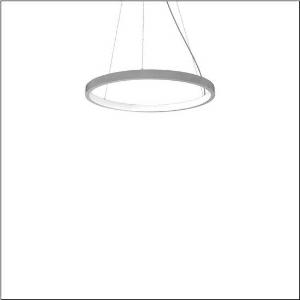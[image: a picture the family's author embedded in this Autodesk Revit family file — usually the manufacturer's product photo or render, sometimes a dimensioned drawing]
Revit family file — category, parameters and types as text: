
# Revit family: silica_21_ring-i_5pjbi2d3204a
name_source: partatom
category: Lighting Fixtures
units: mm (PartAtom-declared; Revit-internal decimal feet)

## family parameters
Cut with Voids When Loaded = No
Host = Face
Light Source = No
Part Type = Normal
Room Calculation Point = No
Round Connector Dimension = Use Diameter
Shared = No

## types (1)
- Silica 21 Ring-I (1 x LED, 5040 lm, 80 W, 4000K)
    Apparent Load = 80 VA
    CIE Flux Codes = 22 48 76 50 101
    Color Rendering = 80
    Color Temperature = 4000K
    Default Elevation = 1800 mm
    Description = Silica 21 Ring-I, suspended luminaire, of PMMA, frosted, light emission: inner ring side luminous distribution, primary light characteristic: symmetric, installation type: suspended mounting, LED, rated luminous flux: 5.040lm, luminous efficacy: 63lm/W, light colour: 840, colour temperature: 4000K, control gear: DALI 2, with terminal, 5-pole, mains connection: 230V, AC/DC, 0/50..60Hz, rated input power: 80W, housing, of extruded aluminium section, metallic grey (RAL 9006), diameter: 805mm, ceiling canopy, metallic grey (RAL 9006), protection rating (lamp compartment): IP40, insulation class (complete): insulation class I (protective earthing), certification: CE, impact resistance: IK02, permissible operating ambient temperature: 0..+35°C, packaging unit: 1 piece
    Height = 48 mm  [stored 0.15748 ft]
    Lamp = 1 x LED
    Lamp Light Flux = 5040 lm
    Lamp Power = 80 W
    Lamp count = 1
    Length = 805 mm
    Luminous efficacy = 63 lm/W
    Manufacturer = Siteco
    ModVariant = No
    Model = 5PJBI2D3204A
    Mounting Place = Ceiling
    Mounting Type = Pendant
    Number of Poles = 1
    OnlyDefault = Yes
    Power Factor = 1
    Product Name = Silica 21 Ring-I
    Product group = suspended luminaire
    ProductGroupID = 904
    Protection Class = Protection class I
    Protection Degree = IP 40
    RLX_Detail_Level = 1
    RLX_Emergency_Light_Flux = 0 lm
    RLX_Emergency_Type = 0
    RLX_Emergency_Type_DB = No
    RlxData = <blob elided: 13109 chars, md5=6e63783a>
    Socket = socket
    Standby Power = 0 W
    System Light Flux = 5040 lm
    System Power = 80 W
    Type Comments = Product without accessories
    Type Image = l_1251752.jpg
    URL = http://relux.com
    VarID = ---
    Voltage = 0 V
    Weight = 0.00 kg
    Width = 0 mm  [stored 0 ft]

note: [stored X ft] marks values corroborated as IEEE doubles in the binary element streams (Revit-internal decimal feet)

## geometry (parser evidence)
native form markers: Sweep x11
no freeform markers — native parametric forms only
